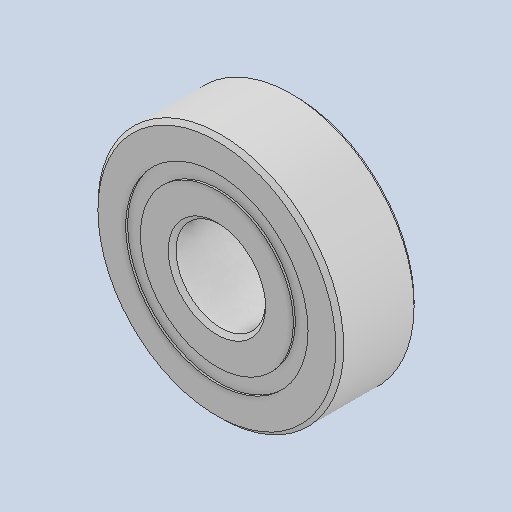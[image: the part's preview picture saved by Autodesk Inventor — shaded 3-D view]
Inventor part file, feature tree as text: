
AUTODESK INVENTOR PART (.ipt)
format: ipt  version: 2023 (Build 270158030, 158C)  size: 587,264 bytes
history: native  units: in
note: dims shown in document units (in); Inventor stores cm internally (conversion verified against a paired STEP export)
features: other x11, revolve x5
ambient origin geometry x8: Origin, YZ Plane, XZ Plane, XY Plane, X Axis, Y Axis, Z Axis, Center Point
bodies: Solid1 (feature_tree), Solid2 (feature_tree), Solid3 (feature_tree), Solid4 (feature_tree), Solid5 (feature_tree), Solid6 (feature_tree), Solid7 (feature_tree), Solid8 (feature_tree), Solid9 (feature_tree), Solid10 (feature_tree), Solid11 (feature_tree), Solid12 (feature_tree), Solid13 (feature_tree), Solid14 (feature_tree), Solid15 (feature_tree), Solid16 (feature_tree)
feature tree (16):
  revolve  "Revolve1"  [1 undecoded]
  revolve  "Revolve3"  [1 undecoded]
  revolve  "Revolve4"  [1 undecoded]
  other  "CirPattern1[1]"
  other  "CirPattern1[2]"
  other  "CirPattern1[3]"
  other  "CirPattern1[4]"
  other  "CirPattern1[5]"
  other  "CirPattern1[6]"
  other  "CirPattern1[7]"
  other  "CirPattern1[8]"
  other  "CirPattern1[9]"
  other  "CirPattern1[10]"
  other  "CirPattern1[11]"
  revolve  "Revolve5[1]"  [1 undecoded]
  revolve  "Revolve5[2]"  [1 undecoded]
note: 5 required parameter values undecoded (feature->parameter linkage not recoverable at this tier; creation-order binding heuristic only, values carry confidence <= 0.55)
